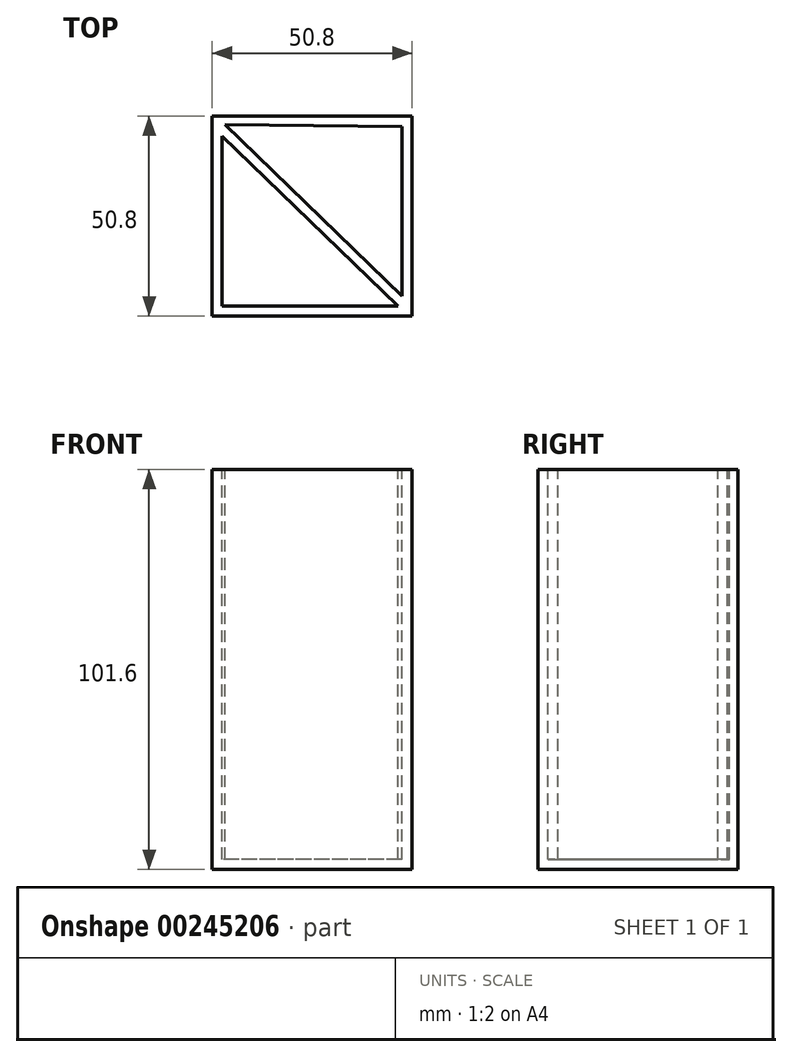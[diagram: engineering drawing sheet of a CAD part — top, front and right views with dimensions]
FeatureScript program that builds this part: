
annotation { "Feature Type Name" : "Feature", "Feature Type Description" : "" }
export const myFeature = defineFeature(function(context is Context, id is Id, definition is map)
    precondition{}
    {
        {
            var Q0;
            Q0=qCreatedBy(makeId("Top.planeOp"),FACE);
            var sketch = newSketch(context, id + "F0", { "sketchPlane" : qUnion([Q0])});
            skLineSegment(sketch, "E0.bottom", {"start": v(0, 0) * mm, "end": v(50.8, 0) * mm});
            skLineSegment(sketch, "E0.top", {"start": v(0, 50.8) * mm, "end": v(50.8, 50.8) * mm});
            skLineSegment(sketch, "E0.left", {"start": v(0, 0) * mm, "end": v(0, 50.8) * mm});
            skLineSegment(sketch, "E0.right", {"start": v(50.8, 0) * mm, "end": v(50.8, 50.8) * mm});
            skSolve(sketch);
        }
        {
            var Q0;
            Q0=makeQuery(id+"F0.imprint","IMPRINT",FACE,{"disambiguationData":[TD([[makeQuery(id+"F0.imprint","IMPRINT",EDGE,{"derivedFrom":sQuery(id+"F0.wireOp",EDGE,"E0.bottom")}),1.0]])]});
            extrude(context, id + "F1", {"entities" : qUnion([Q0]), "depth" : 101.6 * mm});
        }
        {
            var Q0;
            Q0=makeQuery(id+"F1.opExtrude","CAP_FACE",FACE,{"disambiguationData":[OSD([sQuery(id+"F0.wireOp",EDGE,"E0.bottom"),sQuery(id+"F0.wireOp",EDGE,"E0.top"),sQuery(id+"F0.wireOp",EDGE,"E0.left"),sQuery(id+"F0.wireOp",EDGE,"E0.right")])],"isStart":false});
            var sketch = newSketch(context, id + "F2", { "sketchPlane" : qUnion([Q0])});
            skLineSegment(sketch, "E1", {"start": v(2.54, 2.55) * mm, "end": v(2.54, 45.74) * mm});
            skLineSegment(sketch, "E2", {"start": v(2.54, 45.74) * mm, "end": v(47.23, 2.53) * mm});
            skLineSegment(sketch, "E3", {"start": v(47.23, 2.53) * mm, "end": v(2.54, 2.55) * mm});
            skLineSegment(sketch, "E4", {"start": v(3.22, 48.6) * mm, "end": v(48.26, 5.07) * mm});
            skLineSegment(sketch, "E5", {"start": v(48.26, 5.07) * mm, "end": v(48.26, 48.15) * mm});
            skLineSegment(sketch, "E6", {"start": v(48.26, 48.15) * mm, "end": v(3.22, 48.6) * mm});
            skLineSegment(sketch, "E7", {"start": v(2.54, 7.49) * mm, "end": v(0, 7.49) * mm});
            skLineSegment(sketch, "E8", {"start": v(18.16, 2.54) * mm, "end": v(18.16, 0) * mm});
            skLineSegment(sketch, "E9", {"start": v(37.53, 48.26) * mm, "end": v(37.56, 50.8) * mm});
            skLineSegment(sketch, "E10", {"start": v(48.26, 33.18) * mm, "end": v(50.8, 33.18) * mm});
            skLineSegment(sketch, "E11", {"start": v(22.1, 26.82) * mm, "end": v(23.87, 28.64) * mm});
            skSolve(sketch);
        }
        {
            var Q0;
            {var subQ0=sQuery(id+"F2.wireOp",EDGE,"E3");var subQ4=sQuery(id+"F2.wireOp",EDGE,"E1");var subQ7=makeQuery(id+"F2.imprint","INTERSECT",VERTEX,{"derivedFrom":[subQ4,subQ0]});Q0=makeQuery(id+"F2.imprint","IMPRINT",FACE,{"disambiguationData":[TD([[makeQuery(id+"F2.imprint","IMPRINT",EDGE,{"disambiguationData":[TD([[subQ7,-1.0]])],"derivedFrom":subQ4}),-1.0]])]});}
            extrude(context, id + "F3", {"entities" : qUnion([Q0]), "operationType" : NewBodyOperationType.REMOVE, "oppositeDirection" : true, "depth" : 99.06 * mm});
        }
        {
            var Q0;
            {var subQ0=sQuery(id+"F2.wireOp",EDGE,"E6");var subQ4=sQuery(id+"F2.wireOp",EDGE,"E4");var subQ7=makeQuery(id+"F2.imprint","INTERSECT",VERTEX,{"derivedFrom":[subQ4,subQ0]});Q0=makeQuery(id+"F2.imprint","IMPRINT",FACE,{"disambiguationData":[TD([[makeQuery(id+"F2.imprint","IMPRINT",EDGE,{"disambiguationData":[TD([[subQ7,-1.0]])],"derivedFrom":subQ4}),1.0]])]});}
            extrude(context, id + "F4", {"entities" : qUnion([Q0]), "operationType" : NewBodyOperationType.REMOVE, "oppositeDirection" : true, "depth" : 99.06 * mm});
        }
    });
